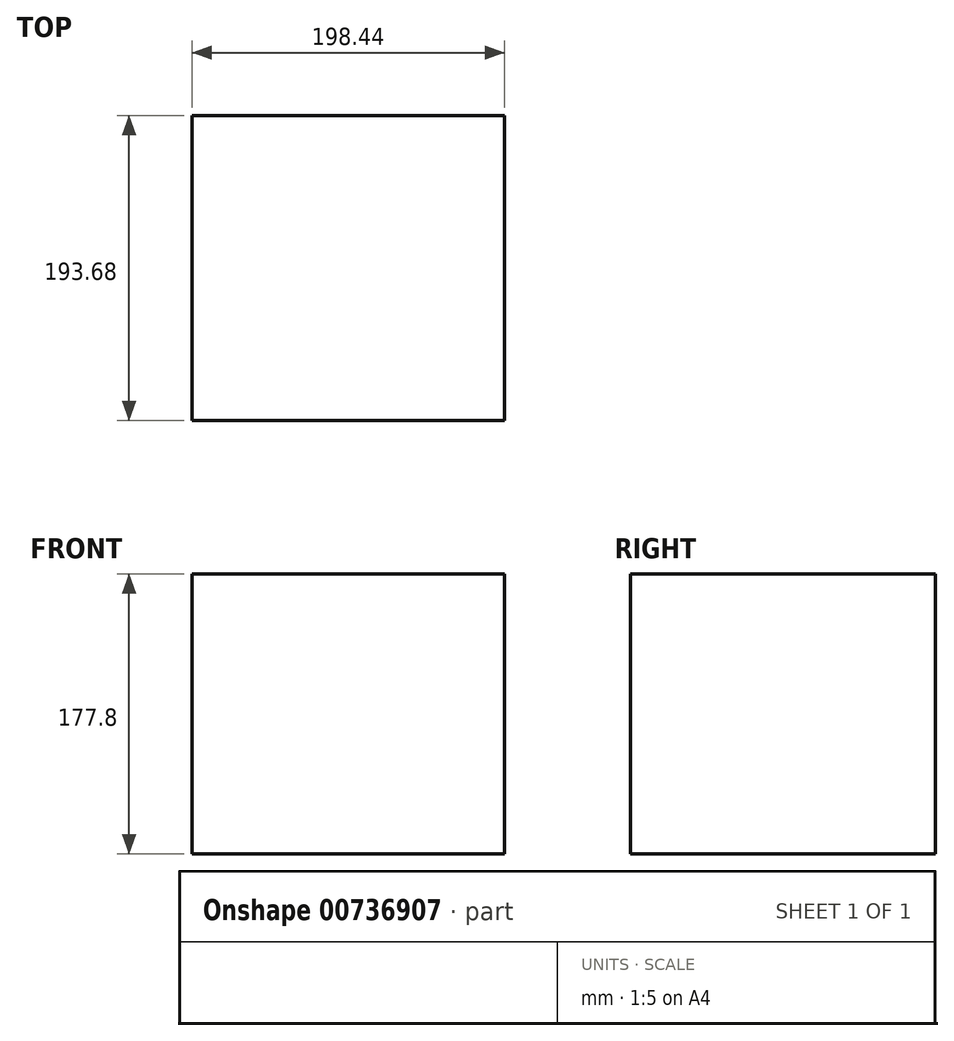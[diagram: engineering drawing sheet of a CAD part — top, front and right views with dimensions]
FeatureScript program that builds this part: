
annotation { "Feature Type Name" : "Feature", "Feature Type Description" : "" }
export const myFeature = defineFeature(function(context is Context, id is Id, definition is map)
    precondition{}
    {
        {
            var Q0;
            Q0=qCreatedBy(makeId("Top.planeOp"),FACE);
            var sketch = newSketch(context, id + "F0", { "sketchPlane" : qUnion([Q0])});
            skLineSegment(sketch, "E0.bottom", {"start": v(0, 0) * mm, "end": v(198.44, 0) * mm});
            skLineSegment(sketch, "E0.top", {"start": v(0, 193.67) * mm, "end": v(198.44, 193.67) * mm});
            skLineSegment(sketch, "E0.left", {"start": v(0, 0) * mm, "end": v(0, 193.67) * mm});
            skLineSegment(sketch, "E0.right", {"start": v(198.44, 0) * mm, "end": v(198.44, 193.67) * mm});
            skSolve(sketch);
        }
        {
            var Q0;
            Q0=makeQuery(id+"F0.imprint","IMPRINT",FACE,{"disambiguationData":[TD([[makeQuery(id+"F0.imprint","IMPRINT",EDGE,{"derivedFrom":sQuery(id+"F0.wireOp",EDGE,"E0.bottom")}),1.0]])]});
            extrude(context, id + "F1", {"entities" : qUnion([Q0]), "depth" : 177.8 * mm, "offsetDistance" : 25.4 * mm});
        }
    });
